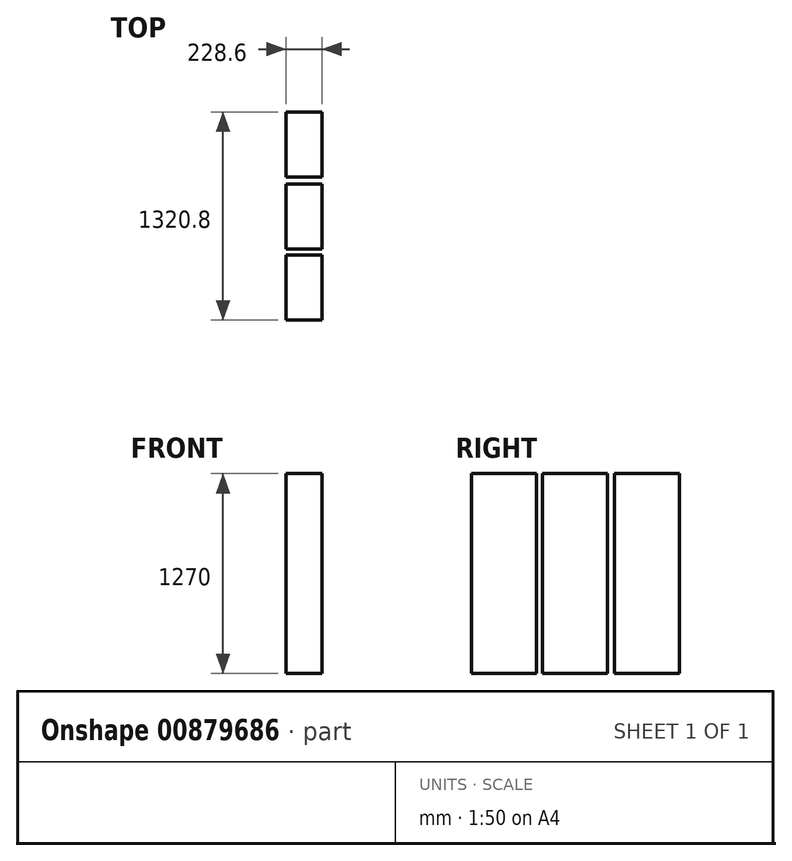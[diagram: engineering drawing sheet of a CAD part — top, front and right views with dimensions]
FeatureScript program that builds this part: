
annotation { "Feature Type Name" : "Feature", "Feature Type Description" : "" }
export const myFeature = defineFeature(function(context is Context, id is Id, definition is map)
    precondition{}
    {
        {
            var Q0;
            Q0=qCreatedBy(makeId("Top.planeOp"),FACE);
            var sketch = newSketch(context, id + "F0", { "sketchPlane" : qUnion([Q0])});
            skLineSegment(sketch, "E0.bottom", {"start": v(-185.39, 420.44) * mm, "end": v(43.21, 420.44) * mm});
            skLineSegment(sketch, "E0.top", {"start": v(-185.39, 7.69) * mm, "end": v(43.21, 7.69) * mm});
            skLineSegment(sketch, "E0.left", {"start": v(-185.39, 420.44) * mm, "end": v(-185.39, 7.69) * mm});
            skLineSegment(sketch, "E0.right", {"start": v(43.21, 420.44) * mm, "end": v(43.21, 7.69) * mm});
            skLineSegment(sketch, "E1.bottom", {"start": v(-185.39, -36.76) * mm, "end": v(43.21, -36.76) * mm});
            skLineSegment(sketch, "E1.top", {"start": v(-185.39, -449.51) * mm, "end": v(43.21, -449.51) * mm});
            skLineSegment(sketch, "E1.left", {"start": v(-185.39, -36.76) * mm, "end": v(-185.39, -449.51) * mm});
            skLineSegment(sketch, "E1.right", {"start": v(43.21, -36.76) * mm, "end": v(43.21, -449.51) * mm});
            skLineSegment(sketch, "E2.bottom", {"start": v(-185.39, -487.61) * mm, "end": v(43.21, -487.61) * mm});
            skLineSegment(sketch, "E2.top", {"start": v(-185.39, -900.36) * mm, "end": v(43.21, -900.36) * mm});
            skLineSegment(sketch, "E2.left", {"start": v(-185.39, -487.61) * mm, "end": v(-185.39, -900.36) * mm});
            skLineSegment(sketch, "E2.right", {"start": v(43.21, -487.61) * mm, "end": v(43.21, -900.36) * mm});
            skSolve(sketch);
        }
        {
            var Q0;
            Q0=makeQuery(id+"F0.imprint","IMPRINT",FACE,{"disambiguationData":[TD([[makeQuery(id+"F0.imprint","IMPRINT",EDGE,{"derivedFrom":sQuery(id+"F0.wireOp",EDGE,"E0.bottom")}),-1.0]])]});
            var Q1;
            Q1=makeQuery(id+"F0.imprint","IMPRINT",FACE,{"disambiguationData":[TD([[makeQuery(id+"F0.imprint","IMPRINT",EDGE,{"derivedFrom":sQuery(id+"F0.wireOp",EDGE,"E1.bottom")}),-1.0]])]});
            var Q2;
            Q2=makeQuery(id+"F0.imprint","IMPRINT",FACE,{"disambiguationData":[TD([[makeQuery(id+"F0.imprint","IMPRINT",EDGE,{"derivedFrom":sQuery(id+"F0.wireOp",EDGE,"E2.bottom")}),-1.0]])]});
            extrude(context, id + "F1", {"entities" : qUnion([Q0, Q1, Q2]), "depth" : 1270 * mm, "offsetDistance" : 25.4 * mm});
        }
    });
